# Revit family: Luminaria Citizen
name_source: partatom
category: Luminarias
revit_build: Autodesk Revit 2016 (Build: 20150220_1215(x64)
units: mm (PartAtom-declared; Revit-internal decimal feet)

## family parameters
Compartido = No
Corte con vacíos al cargar = No
Cota de conector redondo = Diámetro de uso
Número OmniClass = 23.80.70.00
Origen de luz = Sí
Punto de cálculo de habitación = No
Se basa en plano de trabajo = No
Siempre vertical = No
Tipo de pieza = Normal
Título OmniClass = Lighting

## types (1)
- CITIZEN 32 LED 700mA 71W 4000K T5
    Ajuste de potencia = Si
    Alto = 395 mm
    Altura columna = 3-6 m
    Archivo de red fotométrica = ILCZ03245C_CITIZENCOMFORT32LED700mA71W4000KT5-12553.ies
    Cambio de temperatura de color de luz atenuada = <Ninguno>
    Carga aparente = 0 VA
    Certificaciones = CE, ENEC, AENOR, CB SCHEME, RETILAP.
    Clase de aislamiento = Clase I / Clase II
    Classificación = Iluminación
    Comentarios de tipo = Citizen es una luminaria decorativa y eficiente.Buena relación entre eficiencia y coste. Concebida para todo tipo de calles gracias a las combinaciones de potencias y distribuciones fotométricas disponibles.
    Comentarios de vataje = 1
    Descripción = Diseño Urbano decorativo. Excelente disipación térmica. Cubierta de aluminio con disipación pasiva sin aletas. Diseño cut-off y anti deslumbramiento.Difusor de policarbonato de alta calidad ultra transparente de por vida.
    Diametro fijación = Ø 60 mm
    Difusor = Policarbonato
    Diámetro = 500 mm
    Diámetro de círculo de emisión = 400 mm  [stored 1.31234 ft]
    Driver = Incluido
    Fabricante = BENITO
    Ficha tecnica = http://www.benito.com
    Filtro de color = 16777215
    Forma visible en renderización = No
    Frequencia nominal = 50/60 Hz
    Indice de reproducción cromatica = >70
    Instrucciones de montaje = http://www.benito.com
    Lámpara = Led
    Material cuerpo = Cubierta de aluminio
    Modelo = CITIZEN Comfort 32 LED 700 mA 71W 4000K T5
    Peso = 5,5 Kg
    Protección IP = 66
    Protección impacto IK = 10
    Referencia = ILCZ2
    Regulable = Si
    Sistema regulable = SI
    Tipo de opticas = T5
    URL = http://www.benito.com
    URL producto = http://www.benito.com
    Voltage nominal = 220-240 V AC
    Ángulo de inclinación = 90.00°

note: [stored X ft] marks values corroborated as IEEE doubles in the binary element streams (Revit-internal decimal feet)

## geometry (parser evidence)
native form markers: Blend x4
no freeform markers — native parametric forms only
